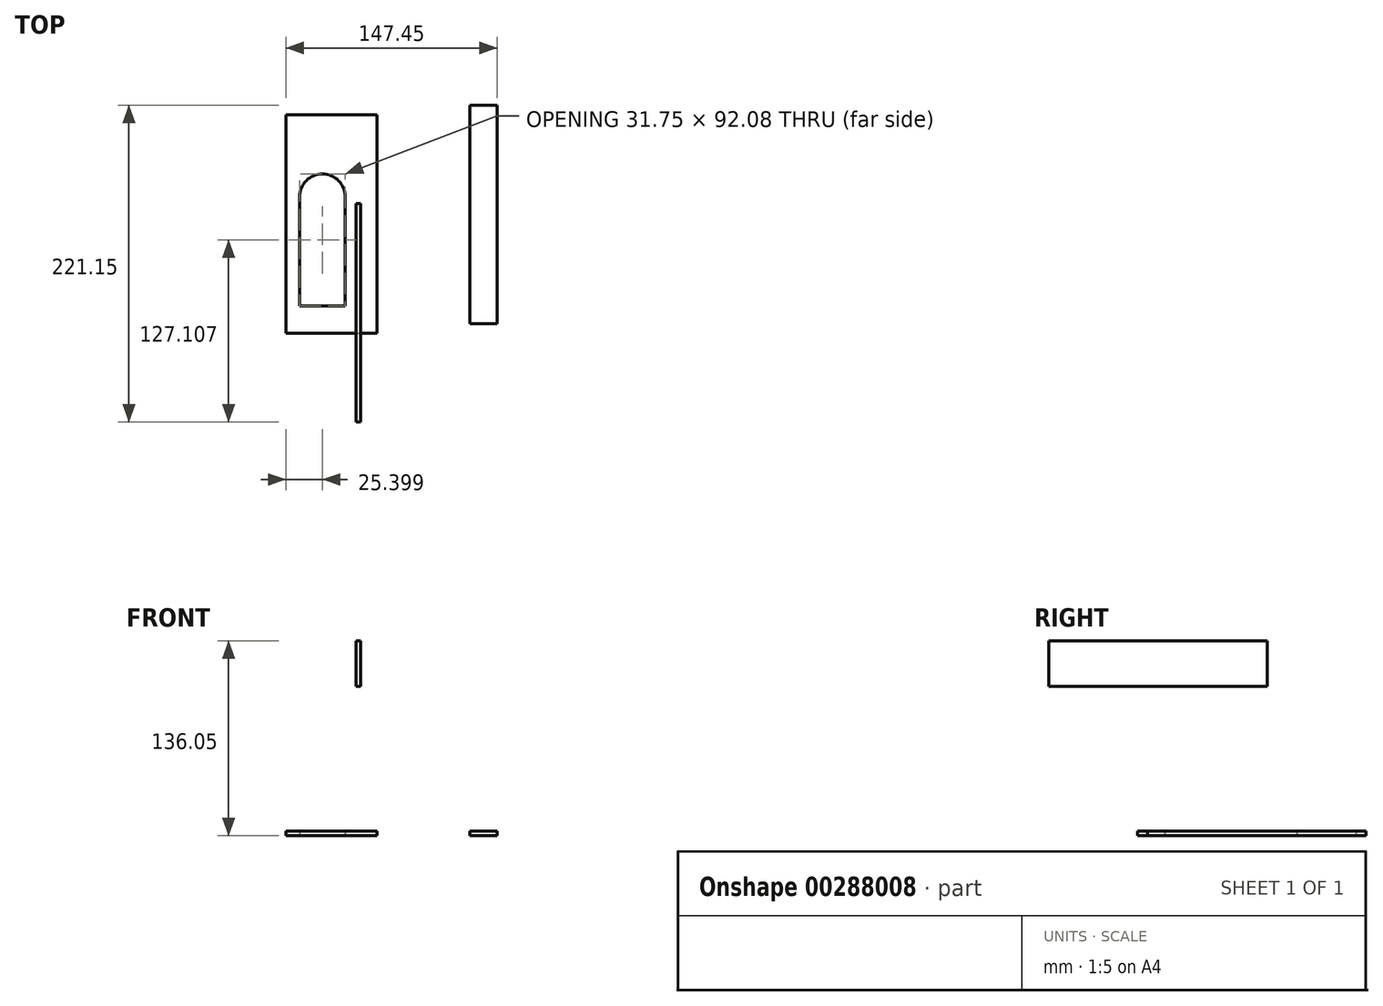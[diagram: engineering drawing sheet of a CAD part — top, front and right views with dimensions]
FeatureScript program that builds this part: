
annotation { "Feature Type Name" : "Feature", "Feature Type Description" : "" }
export const myFeature = defineFeature(function(context is Context, id is Id, definition is map)
    precondition{}
    {
        {
            var Q0;
            Q0=qCreatedBy(makeId("Top.planeOp"),FACE);
            var sketch = newSketch(context, id + "F0", { "sketchPlane" : qUnion([Q0])});
            skLineSegment(sketch, "E0.bottom", {"start": v(-49.05, 118.68) * mm, "end": v(14.45, 118.68) * mm});
            skLineSegment(sketch, "E0.top", {"start": v(-49.05, -33.72) * mm, "end": v(14.45, -33.72) * mm});
            skLineSegment(sketch, "E0.left", {"start": v(-49.05, 118.68) * mm, "end": v(-49.05, -33.72) * mm});
            skLineSegment(sketch, "E0.right", {"start": v(14.45, 118.68) * mm, "end": v(14.45, -33.72) * mm});
            skSolve(sketch);
        }
        {
            var Q0;
            Q0=qCreatedBy(makeId("Top.planeOp"),FACE);
            var sketch = newSketch(context, id + "F1", { "sketchPlane" : qUnion([Q0])});
            skLineSegment(sketch, "E1.bottom", {"start": v(-39.53, 61.53) * mm, "end": v(-7.78, 61.53) * mm});
            skLineSegment(sketch, "E1.top", {"start": v(-39.53, -14.67) * mm, "end": v(-7.78, -14.67) * mm});
            skLineSegment(sketch, "E1.left", {"start": v(-39.53, 61.53) * mm, "end": v(-39.53, -14.67) * mm});
            skLineSegment(sketch, "E1.right", {"start": v(-7.78, 61.53) * mm, "end": v(-7.78, -14.67) * mm});
            skSolve(sketch);
        }
        {
            var Q0;
            Q0=makeQuery(id+"F0.imprint","IMPRINT",FACE,{"disambiguationData":[TD([[makeQuery(id+"F0.imprint","IMPRINT",EDGE,{"derivedFrom":sQuery(id+"F0.wireOp",EDGE,"E0.bottom")}),-1.0]])]});
            extrude(context, id + "F2", {"entities" : qUnion([Q0]), "depth" : 3.12 * mm});
        }
        {
            var Q0;
            Q0=makeQuery(id+"F1.imprint","IMPRINT",FACE,{"disambiguationData":[TD([[makeQuery(id+"F1.imprint","IMPRINT",EDGE,{"derivedFrom":sQuery(id+"F1.wireOp",EDGE,"E1.bottom")}),-1.0]])]});
            extrude(context, id + "F3", {"entities" : qUnion([Q0]), "operationType" : NewBodyOperationType.REMOVE, "depth" : 25.4 * mm});
        }
        {
            var Q0;
            Q0=qCreatedBy(makeId("Top.planeOp"),FACE);
            var sketch = newSketch(context, id + "F4", { "sketchPlane" : qUnion([Q0])});
            skCircle(sketch, "E2", {"center": v(-23.65, 61.53) * mm, "radius": 15.88 * mm});
            skSolve(sketch);
        }
        {
            var Q0;
            Q0=makeQuery(id+"F4.imprint","IMPRINT",FACE,{"disambiguationData":[TD([[makeQuery(id+"F4.imprint","IMPRINT",EDGE,{"derivedFrom":sQuery(id+"F4.wireOp",EDGE,"E2")}),1.0]])]});
            extrude(context, id + "F5", {"entities" : qUnion([Q0]), "operationType" : NewBodyOperationType.REMOVE, "depth" : 25.4 * mm});
        }
        {
            var Q0;
            Q0=qCreatedBy(makeId("Top.planeOp"),FACE);
            var sketch = newSketch(context, id + "F6", { "sketchPlane" : qUnion([Q0])});
            skLineSegment(sketch, "E3.bottom", {"start": v(79.35, 125.4) * mm, "end": v(98.4, 125.4) * mm});
            skLineSegment(sketch, "E3.top", {"start": v(79.35, -27) * mm, "end": v(98.4, -27) * mm});
            skLineSegment(sketch, "E3.left", {"start": v(79.35, 125.4) * mm, "end": v(79.35, -27) * mm});
            skLineSegment(sketch, "E3.right", {"start": v(98.4, 125.4) * mm, "end": v(98.4, -27) * mm});
            skSolve(sketch);
        }
        {
            var Q0;
            Q0 = qSketchRegion(id + "F6", true);
            extrude(context, id + "F7", {"entities" : qUnion([Q0]), "depth" : 3.12 * mm});
        }
        {
            var Q0;
            Q0=qCreatedBy(makeId("Right.planeOp"),FACE);
            var sketch = newSketch(context, id + "F8", { "sketchPlane" : qUnion([Q0])});
            skLineSegment(sketch, "E4.bottom", {"start": v(-95.74, 136.05) * mm, "end": v(56.66, 136.05) * mm});
            skLineSegment(sketch, "E4.top", {"start": v(-95.74, 104.3) * mm, "end": v(56.66, 104.3) * mm});
            skLineSegment(sketch, "E4.left", {"start": v(-95.74, 136.05) * mm, "end": v(-95.74, 104.3) * mm});
            skLineSegment(sketch, "E4.right", {"start": v(56.66, 136.05) * mm, "end": v(56.66, 104.3) * mm});
            skSolve(sketch);
        }
        {
            var Q0;
            Q0 = qSketchRegion(id + "F8", true);
            extrude(context, id + "F9", {"entities" : qUnion([Q0]), "depth" : 3.12 * mm});
        }
    });
